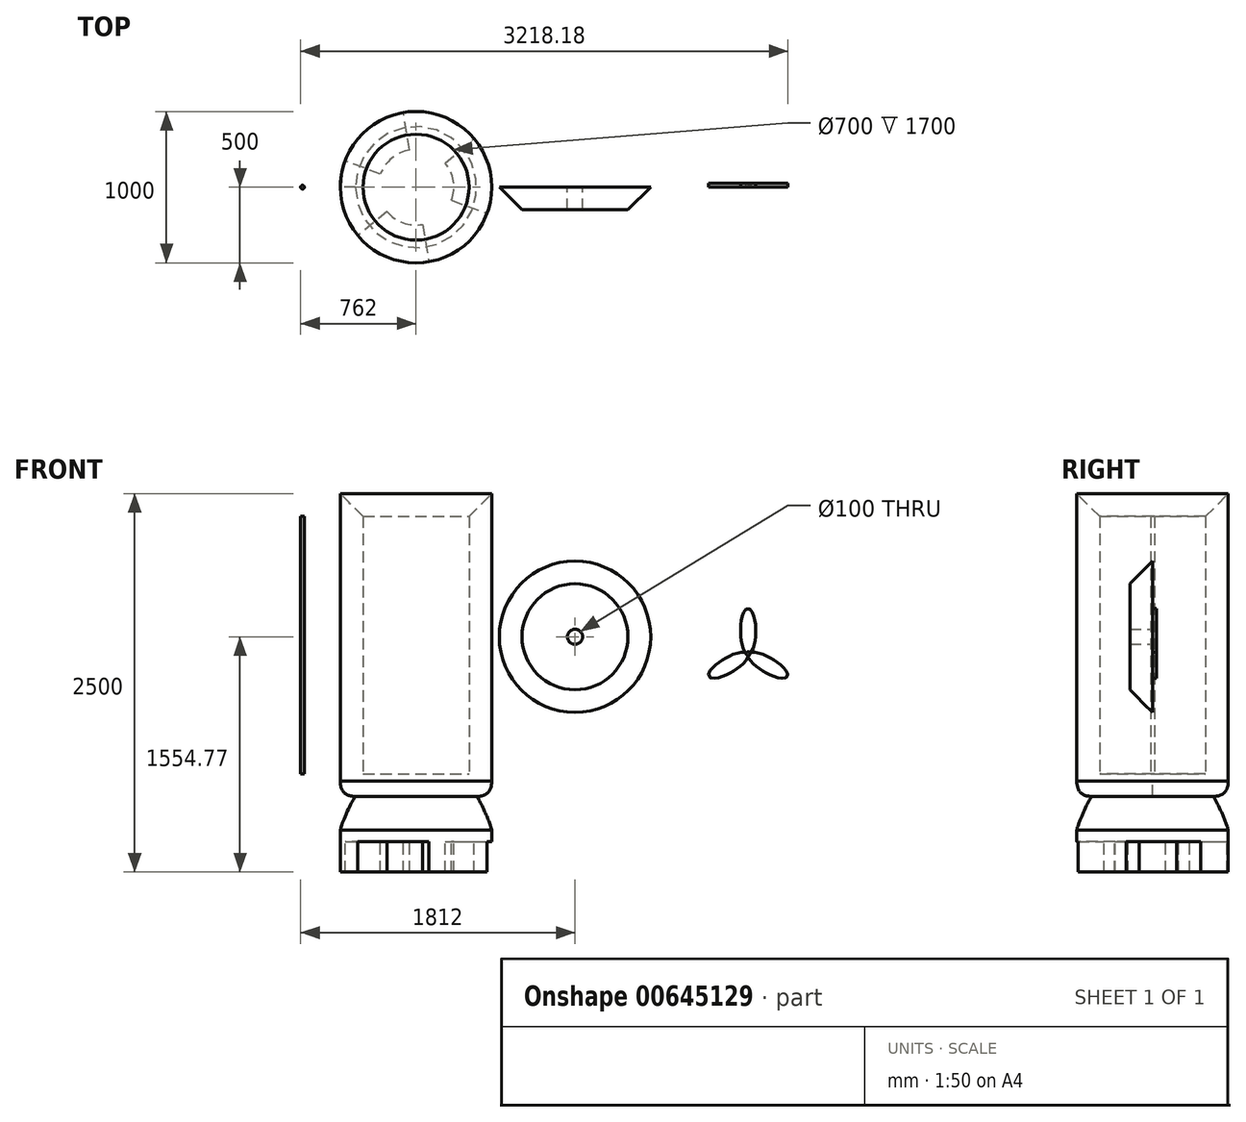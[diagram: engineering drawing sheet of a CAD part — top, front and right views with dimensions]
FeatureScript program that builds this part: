
annotation { "Feature Type Name" : "Feature", "Feature Type Description" : "" }
export const myFeature = defineFeature(function(context is Context, id is Id, definition is map)
    precondition{}
    {
        {
            var Q0;
            Q0=qCreatedBy(makeId("Front.planeOp"),FACE);
            var sketch = newSketch(context, id + "F0", { "sketchPlane" : qUnion([Q0])});
            skLineSegment(sketch, "E0", {"start": v(250, 1000) * mm, "end": v(250, -1000) * mm});
            skLineSegment(sketch, "E1", {"start": v(-250, -1000) * mm, "end": v(250, -1000) * mm});
            skLineSegment(sketch, "E2", {"start": v(-250, -1000) * mm, "end": v(-250, -850) * mm});
            skLineSegment(sketch, "E3", {"start": v(-250, -850) * mm, "end": v(100, -850) * mm});
            skLineSegment(sketch, "E4", {"start": v(100, -850) * mm, "end": v(100, 850) * mm});
            skLineSegment(sketch, "E5", {"start": v(100, 850) * mm, "end": v(250, 1000) * mm});
            skSolve(sketch);
        }
        {
            var Q0;
            Q0=makeQuery(id+"F0.imprint","IMPRINT",FACE,{"disambiguationData":[TD([[makeQuery(id+"F0.imprint","IMPRINT",EDGE,{"derivedFrom":sQuery(id+"F0.wireOp",EDGE,"E0")}),-1.0]])]});
            var Q1;
            Q1=sQuery(id+"F0.wireOp",EDGE,"E2");
            revolve(context, id + "F1", {"entities" : qUnion([Q0]), "axis" : qUnion([Q1]), "revolveType" : RevolveType.ONE_DIRECTION, "angle" : 360 * degree});
        }
        {
            var Q0;
            Q0=makeQuery(id+"F1.opRevolve","SWEPT_EDGE",EDGE,{"disambiguationData":[OSD([sQuery(id+"F0.wireOp",EDGE,"E0"),sQuery(id+"F0.wireOp",EDGE,"E1")])]});
            fillet(context, id + "F2", {"entities" : qUnion([Q0]), "radius" : 100 * mm, "tangentPropagation" : true, "rho" : 0.5, "crossSection" : FilletCrossSection.CONIC, "allowEdgeOverflow" : false});
        }
        {
            var Q0;
            Q0=qCreatedBy(makeId("Front.planeOp"),FACE);
            var sketch = newSketch(context, id + "F3", { "sketchPlane" : qUnion([Q0])});
            skCircle(sketch, "E6", {"center": v(800, 54.77) * mm, "radius": 500 * mm});
            skSolve(sketch);
        }
        {
            var Q0;
            Q0 = qSketchRegion(id + "F3", true);
            extrude(context, id + "F4", {"entities" : qUnion([Q0]), "depth" : 150 * mm, "offsetDistance" : 25 * mm});
        }
        {
            var Q0;
            Q0=makeQuery(id+"F4.opExtrude","CAP_EDGE",EDGE,{"disambiguationData":[OSD([sQuery(id+"F3.wireOp",EDGE,"E6")])],"isStart":false});
            chamfer(context, id + "F5", {"entities" : qUnion([Q0]), "width" : 150 * mm, "tangentPropagation" : true});
        }
        {
            var Q0;
            Q0=makeQuery(id+"F4.opExtrude","CAP_FACE",FACE,{"disambiguationData":[OSD([sQuery(id+"F3.wireOp",EDGE,"E6")])],"isStart":true});
            var sketch = newSketch(context, id + "F6", { "sketchPlane" : qUnion([Q0])});
            skCircle(sketch, "E7", {"center": v(-800, 54.77) * mm, "radius": 50 * mm});
            skSolve(sketch);
        }
        {
            var Q0;
            Q0=sQuery(id+"F6.wireOp",VERTEX,"E7.center");
            var Q1;
            Q1=makeQuery(id+"F4.opExtrude","SWEPT_BODY",BODY,{"disambiguationData":[OSD([sQuery(id+"F3.wireOp",EDGE,"E6")])]});
            hole(context, id + "F7", {"style" : HoleStyle.SIMPLE, "endStyle" : HoleEndStyle.THROUGH, "holeDiameter" : 100 * mm, "majorDiameter" : 5 * mm, "isTappedThrough" : true, "tappedDepth" : 12 * mm, "tapClearance" : 3, "locations" : qUnion([Q0]), "scope" : qUnion([Q1])});
        }
        {
            var Q0;
            Q0=makeQuery(id+"F1.opRevolve","SWEPT_FACE",FACE,{"disambiguationData":[OSD([sQuery(id+"F0.wireOp",EDGE,"E1")])]});
            var sketch = newSketch(context, id + "F8", { "sketchPlane" : qUnion([Q0])});
            skCircle(sketch, "E8", {"center": v(-250, 0) * mm, "radius": 500 * mm});
            skSolve(sketch);
        }
        {
            var Q0;
            Q0 = qSketchRegion(id + "F8", true);
            extrude(context, id + "F9", {"entities" : qUnion([Q0]), "operationType" : NewBodyOperationType.ADD, "depth" : 300 * mm, "offsetDistance" : 25 * mm});
        }
        {
            var Q0;
            Q0=makeQuery(id+"F9.opExtrude","CAP_EDGE",EDGE,{"disambiguationData":[OSD([sQuery(id+"F8.wireOp",EDGE,"E8")])],"isStart":true});
            fillet(context, id + "F10", {"entities" : qUnion([Q0]), "radius" : 300 * mm, "tangentPropagation" : true, "rho" : 0.15, "crossSection" : FilletCrossSection.CONIC, "allowEdgeOverflow" : false});
        }
        {
            var Q0;
            Q0=makeQuery(id+"F9.opExtrude","CAP_FACE",FACE,{"disambiguationData":[OSD([sQuery(id+"F8.wireOp",EDGE,"E8")])],"isStart":false});
            var sketch = newSketch(context, id + "F11", { "sketchPlane" : qUnion([Q0])});
            skArc(sketch, "E9", {"start": v(-334.87, -492.74) * mm, "mid": v(-77.13, -469.16) * mm, "end": v(134.3, -319.87) * mm});
            skLineSegment(sketch, "E10", {"start": v(-442.15, 159.94) * mm, "end": v(-634.3, 319.87) * mm});
            skLineSegment(sketch, "E11", {"start": v(-484.58, -86.44) * mm, "end": v(-719.16, -172.87) * mm});
            skLineSegment(sketch, "E12.1.0", {"start": v(-292.44, -246.37) * mm, "end": v(-334.87, -492.74) * mm});
            skLineSegment(sketch, "E12.1.1", {"start": v(-57.85, -159.94) * mm, "end": v(134.3, -319.87) * mm});
            skCircle(sketch, "E12.1.2", {"center": v(-250, 0) * mm, "radius": 500 * mm});
            skLineSegment(sketch, "E12.2.0", {"start": v(-15.42, 86.44) * mm, "end": v(219.16, 172.87) * mm});
            skLineSegment(sketch, "E12.2.1", {"start": v(-207.56, 246.37) * mm, "end": v(-165.13, 492.74) * mm});
            skArc(sketch, "E12.2.2", {"start": v(-634.3, 319.87) * mm, "mid": v(-77.13, -469.16) * mm, "end": v(-165.13, 492.74) * mm});
            skArc(sketch, "E13", {"start": v(-207.56, 246.37) * mm, "mid": v(-336.44, 234.58) * mm, "end": v(-442.15, 159.94) * mm});
            skArc(sketch, "E14.trimOffspring", {"start": v(-484.58, -86.44) * mm, "mid": v(-409.94, -192.15) * mm, "end": v(-292.44, -246.37) * mm});
            skArc(sketch, "E15.trimOffspring", {"start": v(-57.85, -159.94) * mm, "mid": v(-3.63, -42.44) * mm, "end": v(-15.42, 86.44) * mm});
            skArc(sketch, "E16.trimOffspring", {"start": v(219.16, 172.87) * mm, "mid": v(-422.87, 469.16) * mm, "end": v(-719.16, -172.87) * mm});
            skArc(sketch, "E17", {"start": v(134.3, -319.87) * mm, "mid": v(-77.13, -469.16) * mm, "end": v(-334.87, -492.74) * mm});
            skSolve(sketch);
        }
        {
            var Q0;
            {var subQ4=sQuery(id+"F11.wireOp",EDGE,"E10");Q0=makeQuery(id+"F11.imprint","IMPRINT",FACE,{"disambiguationData":[TD([[makeQuery(id+"F11.imprint","IMPRINT",EDGE,{"derivedFrom":subQ4}),1.0]])]});}
            extrude(context, id + "F12", {"entities" : qUnion([Q0]), "operationType" : NewBodyOperationType.ADD, "depth" : 200 * mm, "offsetDistance" : 25 * mm});
        }
        {
            var Q0;
            Q0=makeQuery(id+"F4.opExtrude","CAP_FACE",FACE,{"disambiguationData":[OSD([sQuery(id+"F3.wireOp",EDGE,"E6")])],"isStart":true});
            var sketch = newSketch(context, id + "F13", { "sketchPlane" : qUnion([Q0])});
            skEllipticalArc(sketch, "E18", {});
            skEllipticalArc(sketch, "E19.1.0", {});
            skEllipticalArc(sketch, "E19.2.0", {});
            skPoint(sketch, "E19.center", {"position": v(-1943.95, -57.71) * mm});
            skCircle(sketch, "E20", {"center": v(-1943.95, -57.71) * mm, "radius": 12.5 * mm});
            const initialGuessF13  = {"E18": [-1.9439523220062256, 0.09228866547346115, 0, 1, 0.15, 0.0504100975940076, 3.5248871516238234, 2.7582981555557673], "E19.1.0": [-2.0738561325738916, -0.13271133452653872, -0.8660254037844388, -0.5, 0.15, 0.0504100975940076, 3.5248871516238163, 2.7582981555557713], "E19.2.0": [-1.8140485114385598, -0.13271133452653872, 0.8660254037844384, -0.5, 0.15, 0.0504100975940076, 3.5248871516238185, 2.7582981555557646]};
            skSetInitialGuess(sketch, initialGuessF13);
            skSolve(sketch);
        }
        {
            var Q0;
            Q0 = qSketchRegion(id + "F13", true);
            extrude(context, id + "F14", {"entities" : qUnion([Q0]), "depth" : 25 * mm, "offsetDistance" : 25 * mm, "hasDraft" : true, "draftAngle" : 3 * degree, "draftPullDirection" : true});
        }
        {
            var Q0;
            Q0=makeQuery(id+"F1.opRevolve","SWEPT_FACE",FACE,{"disambiguationData":[OSD([sQuery(id+"F0.wireOp",EDGE,"E3")])]});
            var sketch = newSketch(context, id + "F15", { "sketchPlane" : qUnion([Q0])});
            skCircle(sketch, "E21", {"center": v(-1000, 0) * mm, "radius": 12 * mm});
            skSolve(sketch);
        }
        {
            var Q0;
            Q0 = qSketchRegion(id + "F15", true);
            extrude(context, id + "F16", {"entities" : qUnion([Q0]), "depth" : 1700 * mm, "offsetDistance" : 25 * mm});
        }
    });
